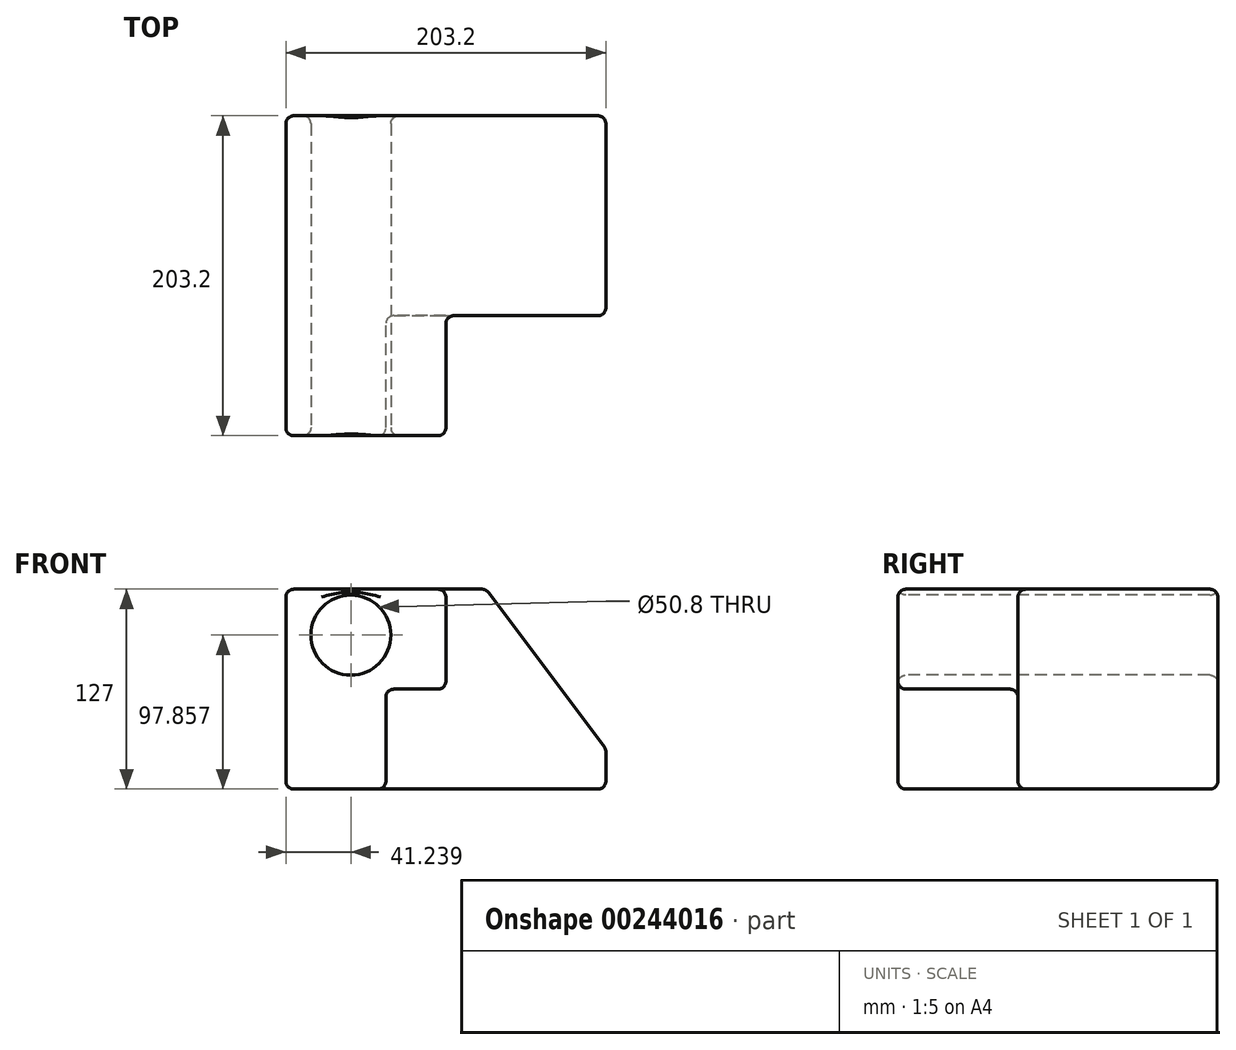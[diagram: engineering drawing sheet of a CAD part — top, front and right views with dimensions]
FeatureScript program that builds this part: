
annotation { "Feature Type Name" : "Feature", "Feature Type Description" : "" }
export const myFeature = defineFeature(function(context is Context, id is Id, definition is map)
    precondition{}
    {
        {
            var Q0;
            Q0=qCreatedBy(makeId("Front.planeOp"),FACE);
            var sketch = newSketch(context, id + "F0", { "sketchPlane" : qUnion([Q0])});
            skLineSegment(sketch, "E0.bottom", {"start": v(101.6, 63.5) * mm, "end": v(-101.6, 63.5) * mm});
            skLineSegment(sketch, "E0.top", {"start": v(101.6, -63.5) * mm, "end": v(-101.6, -63.5) * mm});
            skLineSegment(sketch, "E0.left", {"start": v(101.6, 63.5) * mm, "end": v(101.6, -63.5) * mm});
            skLineSegment(sketch, "E0.right", {"start": v(-101.6, 63.5) * mm, "end": v(-101.6, -63.5) * mm});
            skPoint(sketch, "E0.middle", {"position": v(0, 0) * mm});
            skSolve(sketch);
        }
        {
            var Q0;
            Q0=makeQuery(id+"F0.imprint","IMPRINT",FACE,{"disambiguationData":[TD([[makeQuery(id+"F0.imprint","IMPRINT",EDGE,{"derivedFrom":sQuery(id+"F0.wireOp",EDGE,"E0.bottom")}),1.0]])]});
            extrude(context, id + "F1", {"entities" : qUnion([Q0]), "depth" : 127 * mm});
        }
        {
            var Q0;
            Q0=makeQuery(id+"F1.opExtrude","CAP_FACE",FACE,{"disambiguationData":[OSD([sQuery(id+"F0.wireOp",EDGE,"E0.bottom"),sQuery(id+"F0.wireOp",EDGE,"E0.top"),sQuery(id+"F0.wireOp",EDGE,"E0.left"),sQuery(id+"F0.wireOp",EDGE,"E0.right")])],"isStart":false});
            var sketch = newSketch(context, id + "F2", { "sketchPlane" : qUnion([Q0])});
            skLineSegment(sketch, "E1", {"start": v(-101.6, -63.5) * mm, "end": v(-38.1, -63.5) * mm});
            skLineSegment(sketch, "E2", {"start": v(-38.1, -63.5) * mm, "end": v(-38.1, 0) * mm});
            skLineSegment(sketch, "E3", {"start": v(-38.1, 0) * mm, "end": v(0, 0) * mm});
            skLineSegment(sketch, "E4", {"start": v(0, 0) * mm, "end": v(0, 63.5) * mm});
            skLineSegment(sketch, "E5", {"start": v(0, 63.5) * mm, "end": v(-101.6, 63.5) * mm});
            skLineSegment(sketch, "E6", {"start": v(-101.6, 63.5) * mm, "end": v(-101.6, -63.5) * mm});
            skSolve(sketch);
        }
        {
            var Q0;
            Q0=makeQuery(id+"F2.imprint","IMPRINT",FACE,{"disambiguationData":[TD([[makeQuery(id+"F2.imprint","IMPRINT",EDGE,{"derivedFrom":sQuery(id+"F2.wireOp",EDGE,"E1")}),-1.0]])]});
            extrude(context, id + "F3", {"entities" : qUnion([Q0]), "operationType" : NewBodyOperationType.ADD, "depth" : 76.2 * mm});
        }
        {
            var Q0;
            Q0=makeQuery(id+"F3.opExtrude","CAP_FACE",FACE,{"disambiguationData":[OSD([sQuery(id+"F2.wireOp",EDGE,"E1"),sQuery(id+"F2.wireOp",EDGE,"E2"),sQuery(id+"F2.wireOp",EDGE,"E3"),sQuery(id+"F2.wireOp",EDGE,"E4"),sQuery(id+"F2.wireOp",EDGE,"E5"),sQuery(id+"F2.wireOp",EDGE,"E6")])],"isStart":false});
            var sketch = newSketch(context, id + "F4", { "sketchPlane" : qUnion([Q0])});
            skCircle(sketch, "E7", {"center": v(-60.36, 34.36) * mm, "radius": 17.87 * mm});
            skSolve(sketch);
        }
        {
            var Q0;
            Q0=sQuery(id+"F4.wireOp",VERTEX,"E7.center");
            var Q1;
            Q1=makeQuery(id+"F1.opExtrude","SWEPT_BODY",BODY,{"disambiguationData":[OSD([sQuery(id+"F0.wireOp",EDGE,"E0.bottom"),sQuery(id+"F0.wireOp",EDGE,"E0.top"),sQuery(id+"F0.wireOp",EDGE,"E0.left"),sQuery(id+"F0.wireOp",EDGE,"E0.right")])]});
            hole(context, id + "F5", {"style" : HoleStyle.SIMPLE, "endStyle" : HoleEndStyle.THROUGH, "holeDiameter" : 50.8 * mm, "locations" : qUnion([Q0]), "scope" : qUnion([Q1]), "isTappedThrough" : true});
        }
        {
            var Q0;
            Q0=makeQuery(id+"F1.opExtrude","SWEPT_EDGE",EDGE,{"disambiguationData":[OSD([sQuery(id+"F0.wireOp",EDGE,"E0.bottom"),sQuery(id+"F0.wireOp",EDGE,"E0.left")])]});
            chamfer(context, id + "F6", {"entities" : qUnion([Q0]), "chamferType" : ChamferType.TWO_OFFSETS, "width1" : 76.2 * mm, "oppositeDirection" : false, "width2" : 101.6 * mm, "tangentPropagation" : true});
        }
        {
            var Q0;
            Q0=makeQuery(id+"F5.hole-0.boolean.opBoolean","COPY",EDGE,{"derivedFrom":makeQuery(id+"F5.hole-0.opRevolve","SWEPT_EDGE",EDGE,{"disambiguationData":[OSD([sQuery(id+"F5.hole-0.sketch.wireOp",EDGE,"core_line_2"),sQuery(id+"F5.hole-0.sketch.wireOp",EDGE,"core_line_3")])]})});
            var Q1;
            Q1=makeQuery(id+"F3.opExtrude","SWEPT_FACE",FACE,{"disambiguationData":[OSD([sQuery(id+"F2.wireOp",EDGE,"E3")])]});
            var Q2;
            {var subQ0=sQuery(id+"F0.wireOp",EDGE,"E0.bottom");Q2=makeQuery(id+"F6.opChamfer","BLEND_EDGE",EDGE,{"blendedFrom":[makeQuery(id+"F1.opExtrude","SWEPT_EDGE",EDGE,{"disambiguationData":[OSD([subQ0,sQuery(id+"F0.wireOp",EDGE,"E0.left")])]}),makeQuery(id+"F3.boolean.opBoolean","MERGE",FACE,{"derivedFrom":[makeQuery(id+"F1.opExtrude","SWEPT_FACE",FACE,{"disambiguationData":[OSD([subQ0])]}),makeQuery(id+"F3.opExtrude","SWEPT_FACE",FACE,{"disambiguationData":[OSD([sQuery(id+"F2.wireOp",EDGE,"E5")])]})]})],"blendedInto":[makeQuery(id+"F3.boolean.opBoolean","MERGE",FACE,{"derivedFrom":[makeQuery(id+"F1.opExtrude","SWEPT_FACE",FACE,{"disambiguationData":[OSD([subQ0])]}),makeQuery(id+"F3.opExtrude","SWEPT_FACE",FACE,{"disambiguationData":[OSD([sQuery(id+"F2.wireOp",EDGE,"E5")])]})]})]});}
            var Q3;
            Q3=makeQuery(id+"F3.opExtrude","SWEPT_EDGE",EDGE,{"disambiguationData":[OSD([sQuery(id+"F2.wireOp",EDGE,"E3"),sQuery(id+"F2.wireOp",EDGE,"E4")])]});
            var Q4;
            Q4=makeQuery(id+"F3.opExtrude","SWEPT_EDGE",EDGE,{"disambiguationData":[OSD([sQuery(id+"F0.wireOp",EDGE,"E0.bottom"),sQuery(id+"F2.wireOp",EDGE,"E4"),sQuery(id+"F2.wireOp",EDGE,"E5")])]});
            var Q5;
            Q5=makeQuery(id+"F3.opExtrude","CAP_EDGE",EDGE,{"disambiguationData":[OSD([sQuery(id+"F2.wireOp",EDGE,"E4")])],"isStart":false});
            var Q6;
            Q6=makeQuery(id+"F3.opExtrude","CAP_EDGE",EDGE,{"disambiguationData":[OSD([sQuery(id+"F2.wireOp",EDGE,"E3")])],"isStart":false});
            var Q7;
            Q7=makeQuery(id+"F1.opExtrude","CAP_EDGE",EDGE,{"disambiguationData":[OSD([sQuery(id+"F0.wireOp",EDGE,"E0.bottom")])],"isStart":false});
            var Q8;
            Q8=makeQuery(id+"F5.hole-0.boolean.opBoolean","INTERSECT",EDGE,{"derivedFrom":[makeQuery(id+"F1.opExtrude","CAP_FACE",FACE,{"disambiguationData":[OSD([sQuery(id+"F0.wireOp",EDGE,"E0.bottom"),sQuery(id+"F0.wireOp",EDGE,"E0.top"),sQuery(id+"F0.wireOp",EDGE,"E0.left"),sQuery(id+"F0.wireOp",EDGE,"E0.right")])],"isStart":true}),makeQuery(id+"F5.hole-0.opRevolve","SWEPT_FACE",FACE,{"disambiguationData":[OSD([sQuery(id+"F5.hole-0.sketch.wireOp",EDGE,"core_line_2")])]})]});
            var Q9;
            Q9=makeQuery(id+"F3.opExtrude","SWEPT_FACE",FACE,{"disambiguationData":[OSD([sQuery(id+"F2.wireOp",EDGE,"E4")])]});
            var Q10;
            Q10=makeQuery(id+"F3.opExtrude","CAP_EDGE",EDGE,{"disambiguationData":[OSD([sQuery(id+"F2.wireOp",EDGE,"E4")])],"isStart":true});
            var Q11;
            Q11=makeQuery(id+"F5.hole-0.boolean.opBoolean","COPY",FACE,{"derivedFrom":makeQuery(id+"F5.hole-0.opRevolve","SWEPT_FACE",FACE,{"disambiguationData":[OSD([sQuery(id+"F5.hole-0.sketch.wireOp",EDGE,"core_line_2")])]})});
            var Q12;
            Q12=makeQuery(id+"F3.opExtrude","SWEPT_EDGE",EDGE,{"disambiguationData":[OSD([sQuery(id+"F2.wireOp",EDGE,"E2"),sQuery(id+"F2.wireOp",EDGE,"E3")])]});
            var Q13;
            Q13=makeQuery(id+"F3.opExtrude","CAP_EDGE",EDGE,{"disambiguationData":[OSD([sQuery(id+"F2.wireOp",EDGE,"E3")])],"isStart":true});
            var Q14;
            Q14=makeQuery(id+"F3.boolean.opBoolean","MERGE",EDGE,{"derivedFrom":[makeQuery(id+"F1.opExtrude","SWEPT_EDGE",EDGE,{"disambiguationData":[OSD([sQuery(id+"F0.wireOp",EDGE,"E0.top"),sQuery(id+"F0.wireOp",EDGE,"E0.right")])]}),makeQuery(id+"F3.opExtrude","SWEPT_EDGE",EDGE,{"disambiguationData":[OSD([sQuery(id+"F2.wireOp",EDGE,"E1"),sQuery(id+"F2.wireOp",EDGE,"E6")])]})]});
            var Q15;
            Q15=makeQuery(id+"F3.opExtrude","SWEPT_FACE",FACE,{"disambiguationData":[OSD([sQuery(id+"F2.wireOp",EDGE,"E2")])]});
            var Q16;
            Q16=makeQuery(id+"F1.opExtrude","CAP_FACE",FACE,{"disambiguationData":[OSD([sQuery(id+"F0.wireOp",EDGE,"E0.bottom"),sQuery(id+"F0.wireOp",EDGE,"E0.top"),sQuery(id+"F0.wireOp",EDGE,"E0.left"),sQuery(id+"F0.wireOp",EDGE,"E0.right")])],"isStart":false});
            var Q17;
            Q17=makeQuery(id+"F3.opExtrude","CAP_EDGE",EDGE,{"disambiguationData":[OSD([sQuery(id+"F2.wireOp",EDGE,"E2")])],"isStart":false});
            var Q18;
            Q18=makeQuery(id+"F1.opExtrude","SWEPT_FACE",FACE,{"disambiguationData":[OSD([sQuery(id+"F0.wireOp",EDGE,"E0.left")])]});
            var Q19;
            {var subQ0=sQuery(id+"F0.wireOp",EDGE,"E0.left");var subQ1=sQuery(id+"F0.wireOp",EDGE,"E0.bottom");Q19=makeQuery(id+"F6.opChamfer","BLEND_EDGE",EDGE,{"blendedFrom":[makeQuery(id+"F1.opExtrude","SWEPT_EDGE",EDGE,{"disambiguationData":[OSD([subQ1,subQ0])]}),makeQuery(id+"F1.opExtrude","CAP_FACE",FACE,{"disambiguationData":[OSD([subQ1,sQuery(id+"F0.wireOp",EDGE,"E0.top"),subQ0,sQuery(id+"F0.wireOp",EDGE,"E0.right")])],"isStart":true})],"blendedInto":[makeQuery(id+"F1.opExtrude","CAP_FACE",FACE,{"disambiguationData":[OSD([subQ1,sQuery(id+"F0.wireOp",EDGE,"E0.top"),subQ0,sQuery(id+"F0.wireOp",EDGE,"E0.right")])],"isStart":true})]});}
            var Q20;
            {var subQ0=sQuery(id+"F0.wireOp",EDGE,"E0.left");Q20=makeQuery(id+"F6.opChamfer","BLEND_EDGE",EDGE,{"blendedFrom":[makeQuery(id+"F1.opExtrude","SWEPT_EDGE",EDGE,{"disambiguationData":[OSD([sQuery(id+"F0.wireOp",EDGE,"E0.bottom"),subQ0])]}),makeQuery(id+"F1.opExtrude","SWEPT_FACE",FACE,{"disambiguationData":[OSD([subQ0])]})],"blendedInto":[makeQuery(id+"F1.opExtrude","SWEPT_FACE",FACE,{"disambiguationData":[OSD([subQ0])]})]});}
            var Q21;
            {var subQ0=sQuery(id+"F0.wireOp",EDGE,"E0.left");var subQ1=sQuery(id+"F0.wireOp",EDGE,"E0.bottom");Q21=makeQuery(id+"F6.opChamfer","BLEND_EDGE",EDGE,{"blendedFrom":[makeQuery(id+"F1.opExtrude","SWEPT_EDGE",EDGE,{"disambiguationData":[OSD([subQ1,subQ0])]}),makeQuery(id+"F1.opExtrude","CAP_FACE",FACE,{"disambiguationData":[OSD([subQ1,sQuery(id+"F0.wireOp",EDGE,"E0.top"),subQ0,sQuery(id+"F0.wireOp",EDGE,"E0.right")])],"isStart":false})],"blendedInto":[makeQuery(id+"F1.opExtrude","CAP_FACE",FACE,{"disambiguationData":[OSD([subQ1,sQuery(id+"F0.wireOp",EDGE,"E0.top"),subQ0,sQuery(id+"F0.wireOp",EDGE,"E0.right")])],"isStart":false})]});}
            var Q22;
            Q22=makeQuery(id+"F3.opExtrude","CAP_EDGE",EDGE,{"disambiguationData":[OSD([sQuery(id+"F2.wireOp",EDGE,"E2")])],"isStart":true});
            var Q23;
            Q23=makeQuery(id+"F1.opExtrude","CAP_EDGE",EDGE,{"disambiguationData":[OSD([sQuery(id+"F0.wireOp",EDGE,"E0.top")])],"isStart":true});
            var Q24;
            Q24=makeQuery(id+"F1.opExtrude","CAP_EDGE",EDGE,{"disambiguationData":[OSD([sQuery(id+"F0.wireOp",EDGE,"E0.left")])],"isStart":true});
            var Q25;
            Q25=makeQuery(id+"F3.opExtrude","SWEPT_EDGE",EDGE,{"disambiguationData":[OSD([sQuery(id+"F0.wireOp",EDGE,"E0.top"),sQuery(id+"F2.wireOp",EDGE,"E1"),sQuery(id+"F2.wireOp",EDGE,"E2")])]});
            var Q26;
            Q26=makeQuery(id+"F1.opExtrude","CAP_EDGE",EDGE,{"disambiguationData":[OSD([sQuery(id+"F0.wireOp",EDGE,"E0.top")])],"isStart":false});
            var Q27;
            Q27=makeQuery(id+"F3.boolean.opBoolean","MERGE",FACE,{"derivedFrom":[makeQuery(id+"F1.opExtrude","SWEPT_FACE",FACE,{"disambiguationData":[OSD([sQuery(id+"F0.wireOp",EDGE,"E0.top")])]}),makeQuery(id+"F3.opExtrude","SWEPT_FACE",FACE,{"disambiguationData":[OSD([sQuery(id+"F2.wireOp",EDGE,"E1")])]})]});
            var Q28;
            Q28=makeQuery(id+"F6.opChamfer","BLEND_FACE",FACE,{"disambiguationData":[OSD([sQuery(id+"F0.wireOp",EDGE,"E0.bottom"),sQuery(id+"F0.wireOp",EDGE,"E0.left")])]});
            var Q29;
            Q29=makeQuery(id+"F3.opExtrude","CAP_EDGE",EDGE,{"disambiguationData":[OSD([sQuery(id+"F2.wireOp",EDGE,"E1")])],"isStart":false});
            var Q30;
            Q30=makeQuery(id+"F1.opExtrude","CAP_EDGE",EDGE,{"disambiguationData":[OSD([sQuery(id+"F0.wireOp",EDGE,"E0.left")])],"isStart":false});
            var Q31;
            Q31=makeQuery(id+"F1.opExtrude","SWEPT_EDGE",EDGE,{"disambiguationData":[OSD([sQuery(id+"F0.wireOp",EDGE,"E0.top"),sQuery(id+"F0.wireOp",EDGE,"E0.left")])]});
            var Q32;
            Q32=makeQuery(id+"F3.boolean.opBoolean","MERGE",FACE,{"derivedFrom":[makeQuery(id+"F1.opExtrude","SWEPT_FACE",FACE,{"disambiguationData":[OSD([sQuery(id+"F0.wireOp",EDGE,"E0.bottom")])]}),makeQuery(id+"F3.opExtrude","SWEPT_FACE",FACE,{"disambiguationData":[OSD([sQuery(id+"F2.wireOp",EDGE,"E5")])]})]});
            var Q33;
            Q33=makeQuery(id+"F3.boolean.opBoolean","MERGE",EDGE,{"derivedFrom":[makeQuery(id+"F1.opExtrude","SWEPT_EDGE",EDGE,{"disambiguationData":[OSD([sQuery(id+"F0.wireOp",EDGE,"E0.bottom"),sQuery(id+"F0.wireOp",EDGE,"E0.right")])]}),makeQuery(id+"F3.opExtrude","SWEPT_EDGE",EDGE,{"disambiguationData":[OSD([sQuery(id+"F2.wireOp",EDGE,"E5"),sQuery(id+"F2.wireOp",EDGE,"E6")])]})]});
            var Q34;
            Q34=makeQuery(id+"F3.opExtrude","CAP_EDGE",EDGE,{"disambiguationData":[OSD([sQuery(id+"F2.wireOp",EDGE,"E6")])],"isStart":false});
            var Q35;
            Q35=makeQuery(id+"F3.opExtrude","CAP_FACE",FACE,{"disambiguationData":[OSD([sQuery(id+"F2.wireOp",EDGE,"E1"),sQuery(id+"F2.wireOp",EDGE,"E2"),sQuery(id+"F2.wireOp",EDGE,"E3"),sQuery(id+"F2.wireOp",EDGE,"E4"),sQuery(id+"F2.wireOp",EDGE,"E5"),sQuery(id+"F2.wireOp",EDGE,"E6")])],"isStart":false});
            var Q36;
            Q36=makeQuery(id+"F3.boolean.opBoolean","MERGE",FACE,{"derivedFrom":[makeQuery(id+"F1.opExtrude","SWEPT_FACE",FACE,{"disambiguationData":[OSD([sQuery(id+"F0.wireOp",EDGE,"E0.right")])]}),makeQuery(id+"F3.opExtrude","SWEPT_FACE",FACE,{"disambiguationData":[OSD([sQuery(id+"F2.wireOp",EDGE,"E6")])]})]});
            var Q37;
            Q37=makeQuery(id+"F1.opExtrude","CAP_EDGE",EDGE,{"disambiguationData":[OSD([sQuery(id+"F0.wireOp",EDGE,"E0.bottom")])],"isStart":true});
            var Q38;
            Q38=makeQuery(id+"F3.opExtrude","CAP_EDGE",EDGE,{"disambiguationData":[OSD([sQuery(id+"F2.wireOp",EDGE,"E5")])],"isStart":false});
            var Q39;
            Q39=makeQuery(id+"F1.opExtrude","CAP_FACE",FACE,{"disambiguationData":[OSD([sQuery(id+"F0.wireOp",EDGE,"E0.bottom"),sQuery(id+"F0.wireOp",EDGE,"E0.top"),sQuery(id+"F0.wireOp",EDGE,"E0.left"),sQuery(id+"F0.wireOp",EDGE,"E0.right")])],"isStart":true});
            var Q40;
            Q40=makeQuery(id+"F1.opExtrude","CAP_EDGE",EDGE,{"disambiguationData":[OSD([sQuery(id+"F0.wireOp",EDGE,"E0.right")])],"isStart":true});
            fillet(context, id + "F7", {"entities" : qUnion([Q0, Q1, Q2, Q3, Q4, Q5, Q6, Q7, Q8, Q9, Q10, Q11, Q12, Q13, Q14, Q15, Q16, Q17, Q18, Q19, Q20, Q21, Q22, Q23, Q24, Q25, Q26, Q27, Q28, Q29, Q30, Q31, Q32, Q33, Q34, Q35, Q36, Q37, Q38, Q39, Q40]), "radius" : 5.08 * mm, "tangentPropagation" : true, "allowEdgeOverflow" : false});
        }
    });
